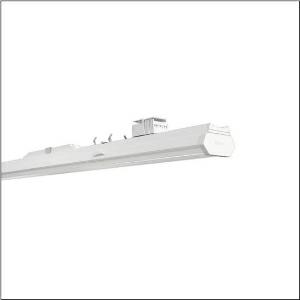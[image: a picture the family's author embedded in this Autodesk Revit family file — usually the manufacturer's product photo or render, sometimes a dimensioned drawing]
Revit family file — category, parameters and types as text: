
# Revit family: licross_11_protected_mo_51tp12dn495gd
name_source: partatom
category: Lighting Fixtures
units: mm (PartAtom-declared; Revit-internal decimal feet)

## family parameters
Cut with Voids When Loaded = No
Host = Face
Light Source = No
Part Type = Normal
Room Calculation Point = No
Round Connector Dimension = Use Diameter
Shared = No

## types (1)
- --- (1 x LED, 1500 lm, 9.3 W, 4000K)
    Apparent Load = 9 VA
    CIE Flux Codes = 73 92 98 99 100
    Color Rendering = 80
    Color Temperature = 4000K
    Default Elevation = 1800 mm
    Description = Licross 11 Protected MO, luminaire insert, of sheet steel, galvanised, coil coated, white, length: 1.500mm, width: 90mm, height: 101mm, LED rated luminous flux: 9.980lm, light colour: 840, SDCM (Standard Deviation of Colour Matching)MacAdam ≤ 2 SDCM (initial), control gear: DALI 2 (for two DALI lines), with plug, 6-pole, with phase selection, mains connection: 220..240V, AC/DC, 0/50..60Hz, rated input power: 57W, internal wiring halogen-free, for central battery installations according to EN 60598-2-22, for emergency light function, without changeover relay, primary optical cover: cover, of PMMA, light emission: direct distribution, primary light characteristic: symmetric, protection rating (complete): IP64, insulation class (complete): insulation class I (protective earthing), certification: CE, ENEC, VDE, UKCA, protection symbol: D if used in an environment with conductive dust loads with corresponding accessories, impact resistance: IK06, permissible ambient temperature for indoor applications: -25..+35°C, standard: EN 60598-2-22, corresponds to IFS (International Featured Standards) requirements for safety and quality in the food industry, reducing of maximum allowable ambient temperature of 5°C with ceiling mounting, LABS conformity tested according to VDMA 24364:2018-05, The light source and the operating device comply with the requirements of the Ecodesign Regulation (EU) 2019/2020 and are replaceable in accordance with this regulation, packaging unit: 1 piece
    Height = 92 mm
    Lamp = 1 x LED
    Lamp Light Flux = 1500 lm
    Lamp Power = 9.3 W
    Lamp count = 1
    Length = 1500 mm  [stored 4.92126 ft]
    Luminous efficacy = 161 lm/W
    Manufacturer = Siteco
    ModVariant = No
    Model = 51TP12DN495GD
    Mounting Place = Ceiling
    Mounting Type = Pendant
    Number of Poles = 1
    OnlyDefault = Yes
    Power Factor = 1
    Product Name = Licross 11 Protected MO
    Product group = luminaire insert | ceiling pendant
    ProductGroupID = 901
    Protection Class = Protection class I
    Protection Degree = IP 64
    RLX_Detail_Level = 1
    RLX_Emergency_Light_Flux = 0 lm
    RLX_Emergency_Type = 0
    RLX_Emergency_Type_DB = No
    RlxData = <blob elided: 25217 chars, md5=a2df39db>
    Socket = socket
    Standby Power = 0 W
    System Light Flux = 1500 lm
    System Power = 9 W
    Type Comments = : DC mode (central or group accumulator) initial emergency light level
    Type Image = l_1256148.jpg
    URL = http://relux.com
    VarID = @adj_091573
    Voltage = 0 V
    Weight = 0.00 kg
    Width = 88 mm

note: [stored X ft] marks values corroborated as IEEE doubles in the binary element streams (Revit-internal decimal feet)

## geometry (parser evidence)
native form markers: Blend x4, Sweep x10
no freeform markers — native parametric forms only
